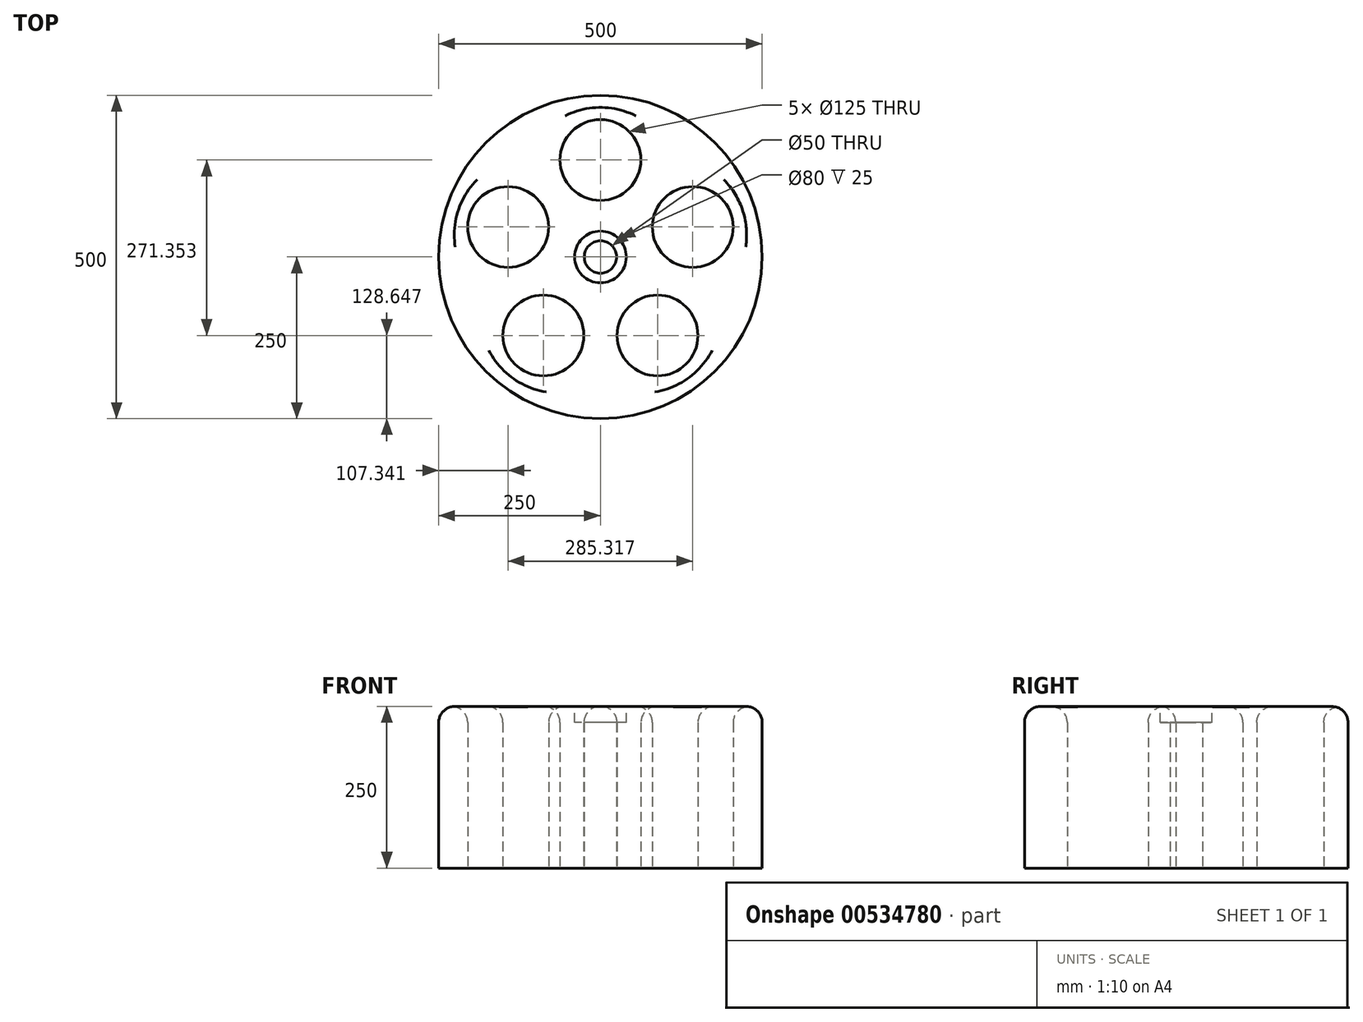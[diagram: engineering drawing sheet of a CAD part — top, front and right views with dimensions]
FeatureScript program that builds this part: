
annotation { "Feature Type Name" : "Feature", "Feature Type Description" : "" }
export const myFeature = defineFeature(function(context is Context, id is Id, definition is map)
    precondition{}
    {
        {
            var Q0;
            Q0=qCreatedBy(makeId("Top.planeOp"),FACE);
            var sketch = newSketch(context, id + "F0", { "sketchPlane" : qUnion([Q0])});
            skCircle(sketch, "E0", {"center": v(0, 0) * mm, "radius": 250 * mm});
            skCircle(sketch, "E1", {"center": v(0, 150) * mm, "radius": 62.5 * mm});
            skCircle(sketch, "E2.1.0", {"center": v(-142.66, 46.35) * mm, "radius": 62.5 * mm});
            skCircle(sketch, "E2.2.0", {"center": v(-88.17, -121.35) * mm, "radius": 62.5 * mm});
            skCircle(sketch, "E2.3.0", {"center": v(88.17, -121.35) * mm, "radius": 62.5 * mm});
            skCircle(sketch, "E2.4.0", {"center": v(142.66, 46.35) * mm, "radius": 62.5 * mm});
            skCircle(sketch, "E3", {"center": v(0, 0) * mm, "radius": 25 * mm});
            skSolve(sketch);
        }
        {
            var Q0;
            Q0=makeQuery(id+"F0.imprint","IMPRINT",FACE,{"disambiguationData":[TD([[makeQuery(id+"F0.imprint","IMPRINT",EDGE,{"derivedFrom":sQuery(id+"F0.wireOp",EDGE,"E0")}),1.0]])]});
            extrude(context, id + "F1", {"entities" : qUnion([Q0]), "depth" : 250 * mm, "offsetDistance" : 25 * mm});
        }
        {
            var Q0;
            Q0=makeQuery(id+"F1.opExtrude","CAP_EDGE",EDGE,{"disambiguationData":[OSD([sQuery(id+"F0.wireOp",EDGE,"E2.2.0")])],"isStart":false});
            var Q1;
            Q1=makeQuery(id+"F1.opExtrude","CAP_EDGE",EDGE,{"disambiguationData":[OSD([sQuery(id+"F0.wireOp",EDGE,"E2.1.0")])],"isStart":false});
            var Q2;
            Q2=makeQuery(id+"F1.opExtrude","CAP_EDGE",EDGE,{"disambiguationData":[OSD([sQuery(id+"F0.wireOp",EDGE,"E1")])],"isStart":false});
            var Q3;
            Q3=makeQuery(id+"F1.opExtrude","CAP_EDGE",EDGE,{"disambiguationData":[OSD([sQuery(id+"F0.wireOp",EDGE,"E2.4.0")])],"isStart":false});
            var Q4;
            Q4=makeQuery(id+"F1.opExtrude","CAP_EDGE",EDGE,{"disambiguationData":[OSD([sQuery(id+"F0.wireOp",EDGE,"E2.3.0")])],"isStart":false});
            var Q5;
            Q5=makeQuery(id+"F1.opExtrude","CAP_EDGE",EDGE,{"disambiguationData":[OSD([sQuery(id+"F0.wireOp",EDGE,"E0")])],"isStart":false});
            fillet(context, id + "F2", {"entities" : qUnion([Q0, Q1, Q2, Q3, Q4, Q5]), "radius" : 25 * mm, "tangentPropagation" : true, "allowEdgeOverflow" : false});
        }
        {
            var Q0;
            Q0=makeQuery(id+"F1.opExtrude","CAP_FACE",FACE,{"disambiguationData":[OSD([sQuery(id+"F0.wireOp",EDGE,"E0"),sQuery(id+"F0.wireOp",EDGE,"E1"),sQuery(id+"F0.wireOp",EDGE,"E2.1.0"),sQuery(id+"F0.wireOp",EDGE,"E2.2.0"),sQuery(id+"F0.wireOp",EDGE,"E2.3.0"),sQuery(id+"F0.wireOp",EDGE,"E2.4.0"),sQuery(id+"F0.wireOp",EDGE,"E3")])],"isStart":false});
            var sketch = newSketch(context, id + "F3", { "sketchPlane" : qUnion([Q0])});
            skCircle(sketch, "E4", {"center": v(0, 0) * mm, "radius": 40 * mm});
            skSolve(sketch);
        }
        {
            var Q0;
            Q0 = qSketchRegion(id + "F3", true);
            extrude(context, id + "F4", {"entities" : qUnion([Q0]), "operationType" : NewBodyOperationType.REMOVE, "oppositeDirection" : true, "depth" : 25 * mm, "offsetDistance" : 25 * mm});
        }
    });
